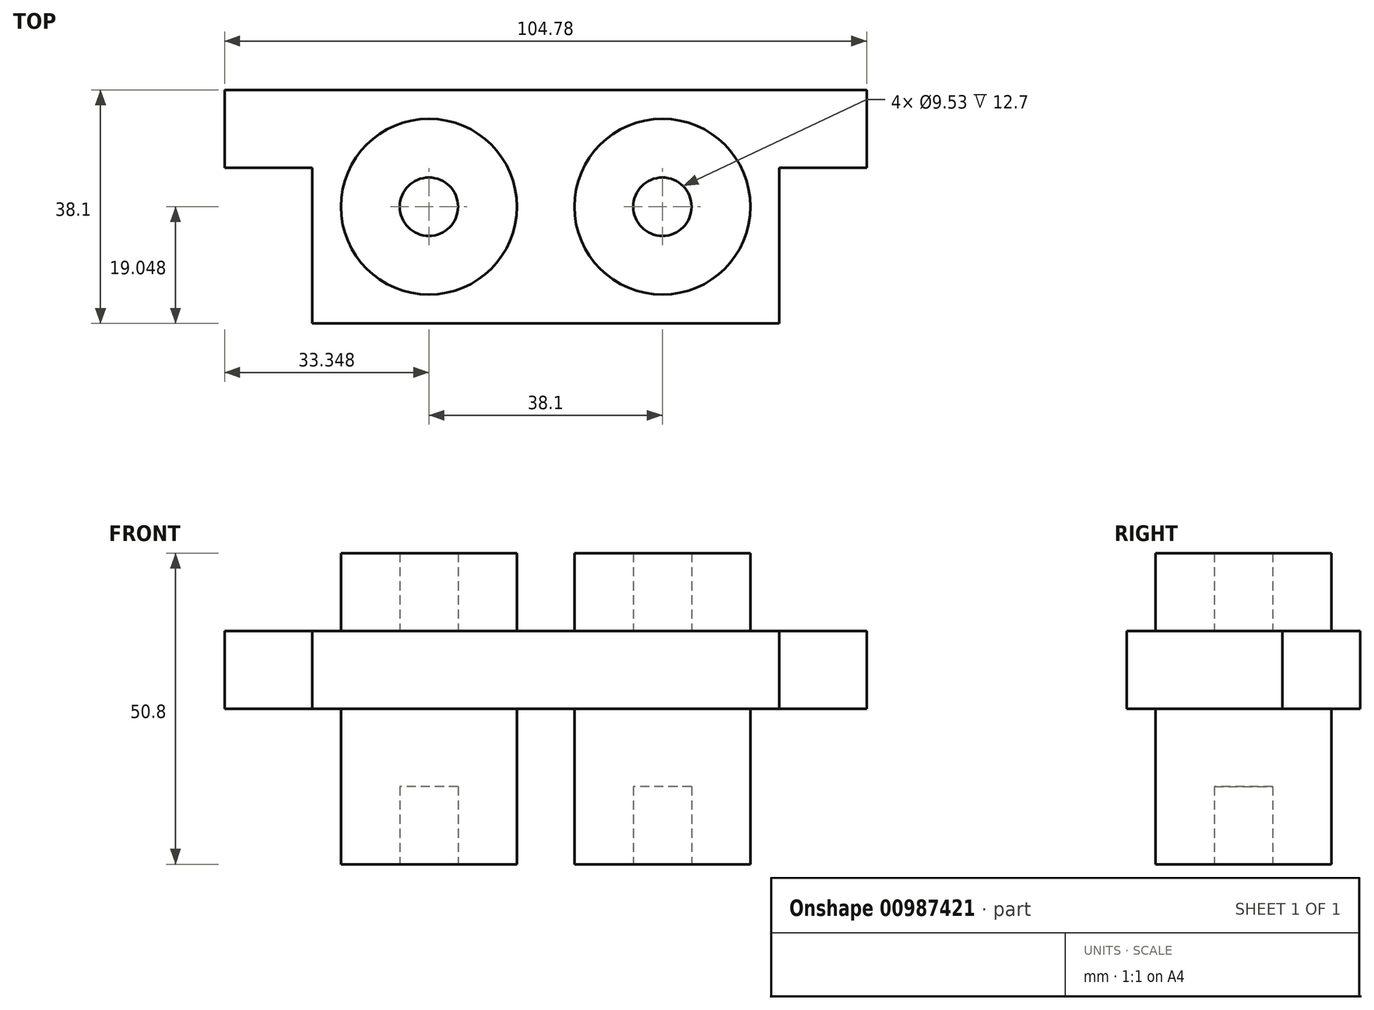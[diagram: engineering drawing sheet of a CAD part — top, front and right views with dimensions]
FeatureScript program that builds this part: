
annotation { "Feature Type Name" : "Feature", "Feature Type Description" : "" }
export const myFeature = defineFeature(function(context is Context, id is Id, definition is map)
    precondition{}
    {
        {
            var Q0;
            Q0=qCreatedBy(makeId("Top.planeOp"),FACE);
            var sketch = newSketch(context, id + "F0", { "sketchPlane" : qUnion([Q0])});
            skCircle(sketch, "E0", {"center": v(-25.15, -30.63) * mm, "radius": 14.35 * mm});
            skCircle(sketch, "E1", {"center": v(-25.15, -30.63) * mm, "radius": 4.76 * mm});
            skCircle(sketch, "E2", {"center": v(12.95, -30.63) * mm, "radius": 14.35 * mm});
            skCircle(sketch, "E3", {"center": v(12.95, -30.63) * mm, "radius": 4.76 * mm});
            skLineSegment(sketch, "E4.top", {"start": v(-44.2, -49.68) * mm, "end": v(32, -49.68) * mm});
            skLineSegment(sketch, "E5.top", {"start": v(-58.5, -24.28) * mm, "end": v(-44.2, -24.28) * mm});
            skLineSegment(sketch, "E5.left", {"start": v(-58.5, -11.58) * mm, "end": v(-58.5, -24.28) * mm});
            skLineSegment(sketch, "E6.top", {"start": v(32, -24.28) * mm, "end": v(46.28, -24.28) * mm});
            skLineSegment(sketch, "E6.right", {"start": v(46.28, -11.58) * mm, "end": v(46.28, -24.28) * mm});
            skLineSegment(sketch, "E7", {"start": v(-44.2, -49.68) * mm, "end": v(-44.2, -24.28) * mm});
            skLineSegment(sketch, "E8", {"start": v(32, -49.68) * mm, "end": v(32, -24.28) * mm});
            skLineSegment(sketch, "E9", {"start": v(-58.5, -11.58) * mm, "end": v(46.28, -11.58) * mm});
            skSolve(sketch);
        }
        {
            var Q0;
            Q0=makeQuery(id+"F0.imprint","IMPRINT",FACE,{"disambiguationData":[TD([[makeQuery(id+"F0.imprint","IMPRINT",EDGE,{"derivedFrom":sQuery(id+"F0.wireOp",EDGE,"E0")}),-1.0]])]});
            extrude(context, id + "F1", {"entities" : qUnion([Q0]), "depth" : 12.7 * mm, "offsetDistance" : 25.4 * mm});
        }
        {
            var Q0;
            Q0=makeQuery(id+"F0.imprint","IMPRINT",FACE,{"disambiguationData":[TD([[makeQuery(id+"F0.imprint","IMPRINT",EDGE,{"derivedFrom":sQuery(id+"F0.wireOp",EDGE,"E0")}),1.0]])]});
            var Q1;
            Q1=makeQuery(id+"F0.imprint","IMPRINT",FACE,{"disambiguationData":[TD([[makeQuery(id+"F0.imprint","IMPRINT",EDGE,{"derivedFrom":sQuery(id+"F0.wireOp",EDGE,"E2")}),1.0]])]});
            extrude(context, id + "F2", {"entities" : qUnion([Q0, Q1]), "operationType" : NewBodyOperationType.ADD, "depth" : 25.4 * mm, "offsetDistance" : 25.4 * mm, "hasSecondDirection" : true, "secondDirectionOppositeDirection" : true, "secondDirectionDepth" : 25.4 * mm});
        }
        {
            var Q0;
            Q0=makeQuery(id+"F0.imprint","IMPRINT",FACE,{"disambiguationData":[TD([[makeQuery(id+"F0.imprint","IMPRINT",EDGE,{"derivedFrom":sQuery(id+"F0.wireOp",EDGE,"E1")}),1.0]])]});
            var Q1;
            Q1=makeQuery(id+"F0.imprint","IMPRINT",FACE,{"disambiguationData":[TD([[makeQuery(id+"F0.imprint","IMPRINT",EDGE,{"derivedFrom":sQuery(id+"F0.wireOp",EDGE,"E3")}),1.0]])]});
            extrude(context, id + "F3", {"entities" : qUnion([Q0, Q1]), "operationType" : NewBodyOperationType.ADD, "depth" : 12.7 * mm, "offsetDistance" : 25.4 * mm, "hasSecondDirection" : true, "secondDirectionOppositeDirection" : true, "secondDirectionDepth" : 12.7 * mm});
        }
    });
